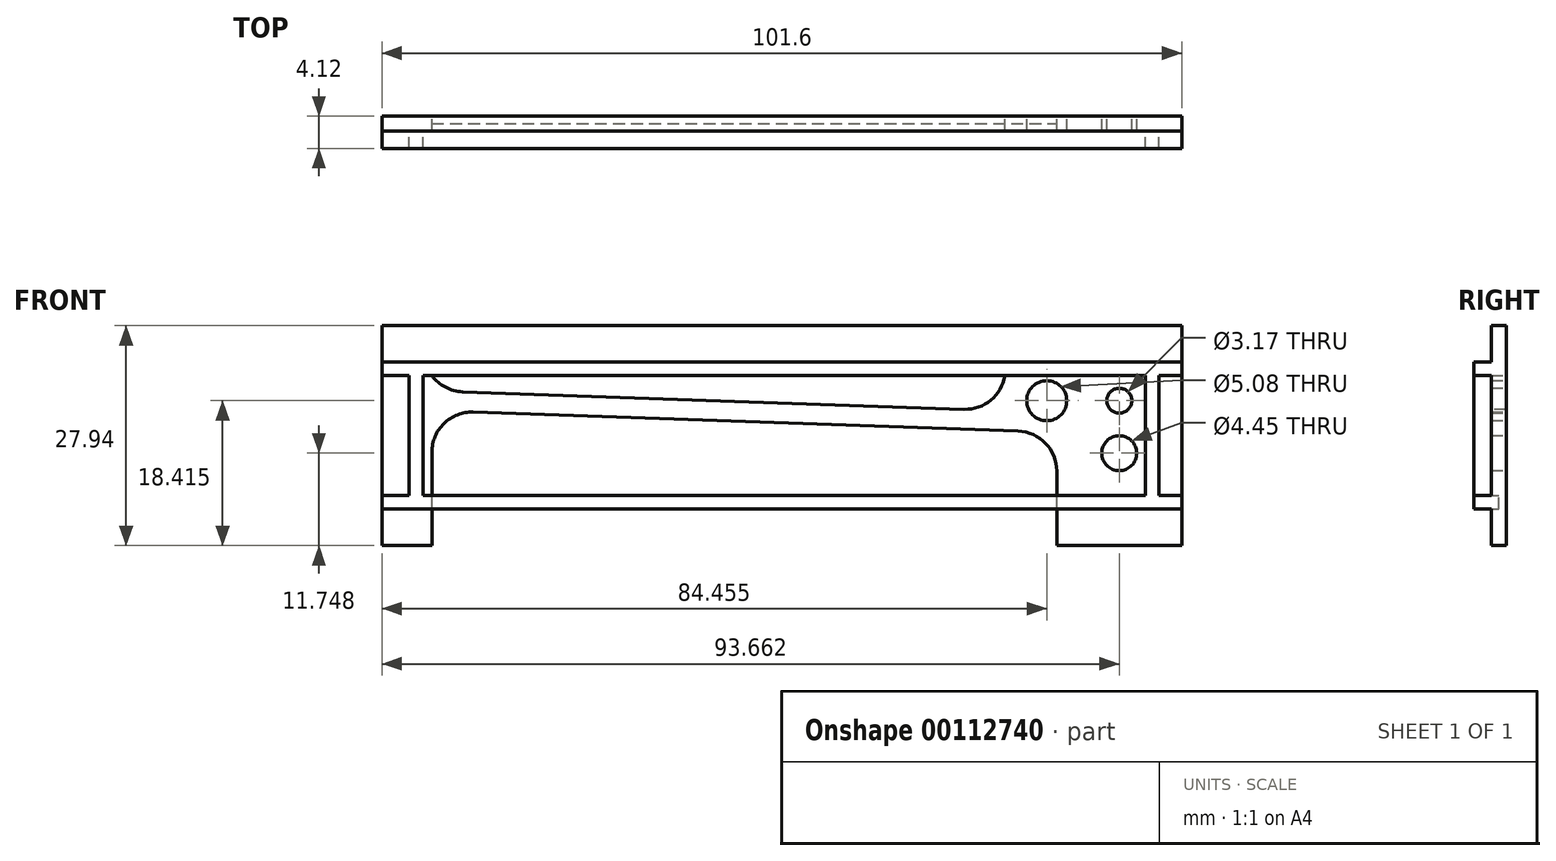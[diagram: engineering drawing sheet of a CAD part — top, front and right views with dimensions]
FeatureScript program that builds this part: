
annotation { "Feature Type Name" : "Feature", "Feature Type Description" : "" }
export const myFeature = defineFeature(function(context is Context, id is Id, definition is map)
    precondition{}
    {
        {
            var Q0;
            Q0=qCreatedBy(makeId("Front.planeOp"),FACE);
            var sketch = newSketch(context, id + "F0", { "sketchPlane" : qUnion([Q0])});
            skLineSegment(sketch, "E0.bottom", {"start": v(-50.8, 0) * mm, "end": v(50.8, 0) * mm});
            skLineSegment(sketch, "E0.top", {"start": v(-50.8, 27.94) * mm, "end": v(50.8, 27.94) * mm});
            skLineSegment(sketch, "E0.left", {"start": v(-50.8, 0) * mm, "end": v(-50.8, 27.94) * mm});
            skLineSegment(sketch, "E0.right", {"start": v(50.8, 0) * mm, "end": v(50.8, 27.94) * mm});
            skLineSegment(sketch, "E1.left", {"start": v(-44.45, 0) * mm, "end": v(-44.45, 17.15) * mm});
            skLineSegment(sketch, "E1.right", {"start": v(34.92, 0) * mm, "end": v(34.92, 14.37) * mm});
            skLineSegment(sketch, "E2", {"start": v(58.26, 4.45) * mm, "end": v(77.64, 4.45) * mm, "construction": true});
            skLineSegment(sketch, "E3", {"start": v(58.26, 23.5) * mm, "end": v(77.64, 23.5) * mm, "construction": true});
            skLineSegment(sketch, "E4", {"start": v(34.93, 14.37) * mm, "end": v(-44.45, 17.14) * mm});
            skLineSegment(sketch, "E5.bottom", {"start": v(-44.45, 0) * mm, "end": v(34.92, 0) * mm});
            skLineSegment(sketch, "E5.top", {"start": v(-44.45, 6.35) * mm, "end": v(34.92, 6.35) * mm});
            skLineSegment(sketch, "E5.left", {"start": v(-44.45, 0) * mm, "end": v(-44.45, 6.35) * mm});
            skLineSegment(sketch, "E5.right", {"start": v(34.92, 0) * mm, "end": v(34.92, 6.35) * mm});
            skLineSegment(sketch, "E6", {"start": v(0, -5.2) * mm, "end": v(0, 26.47) * mm, "construction": true});
            skCircle(sketch, "E7", {"center": v(42.86, 18.42) * mm, "radius": 1.59 * mm});
            skLineSegment(sketch, "E8", {"start": v(28.33, 21.6) * mm, "end": v(-44.45, 21.59) * mm});
            skLineSegment(sketch, "E9", {"start": v(-44.45, 21.59) * mm, "end": v(-44.45, 19.69) * mm});
            skLineSegment(sketch, "E10", {"start": v(-44.45, 19.69) * mm, "end": v(28.33, 17.15) * mm});
            skLineSegment(sketch, "E11", {"start": v(28.33, 17.15) * mm, "end": v(28.33, 21.6) * mm});
            skCircle(sketch, "E12", {"center": v(33.66, 18.42) * mm, "radius": 2.54 * mm});
            skCircle(sketch, "E13", {"center": v(42.86, 11.75) * mm, "radius": 2.22 * mm});
            skSolve(sketch);
        }
        {
            var Q0;
            Q0=makeQuery(id+"F0.imprint","IMPRINT",FACE,{"disambiguationData":[TD([[makeQuery(id+"F0.imprint","IMPRINT",EDGE,{"derivedFrom":sQuery(id+"F0.wireOp",EDGE,"E0.top")}),-1.0]])]});
            var Q1;
            Q1=makeQuery(id+"F0.imprint","IMPRINT",FACE,{"disambiguationData":[TD([[makeQuery(id+"F0.imprint","IMPRINT",EDGE,{"derivedFrom":sQuery(id+"F0.wireOp",EDGE,"FsuTxIii-Xo9e-dLFT-zOUX-yXm8lsklTmyg.bottom")}),-1.0]])]});
            var Q2;
            Q2=makeQuery(id+"F0.imprint","IMPRINT",FACE,{"disambiguationData":[TD([[makeQuery(id+"F0.imprint","IMPRINT",EDGE,{"derivedFrom":sQuery(id+"F0.wireOp",EDGE,"E5.bottom")}),1.0]])]});
            extrude(context, id + "F1", {"entities" : qUnion([Q0, Q1, Q2]), "depth" : 1.9 * mm, "symmetric" : true});
        }
        {
            var Q0;
            Q0=makeQuery(id+"F1.opExtrude","SWEPT_EDGE",EDGE,{"disambiguationData":[OSD([sQuery(id+"F0.wireOp",EDGE,"E1.left"),sQuery(id+"F0.wireOp",EDGE,"E4")])]});
            var Q1;
            Q1=makeQuery(id+"F1.opExtrude","SWEPT_EDGE",EDGE,{"disambiguationData":[OSD([sQuery(id+"F0.wireOp",EDGE,"E1.right"),sQuery(id+"F0.wireOp",EDGE,"E4")])]});
            var Q2;
            Q2=makeQuery(id+"F1.opExtrude","SWEPT_EDGE",EDGE,{"disambiguationData":[OSD([sQuery(id+"F0.wireOp",EDGE,"E9"),sQuery(id+"F0.wireOp",EDGE,"E10")])]});
            var Q3;
            Q3=makeQuery(id+"F1.opExtrude","SWEPT_EDGE",EDGE,{"disambiguationData":[OSD([sQuery(id+"F0.wireOp",EDGE,"E10"),sQuery(id+"F0.wireOp",EDGE,"E11")])]});
            fillet(context, id + "F2", {"entities" : qUnion([Q0, Q1, Q2, Q3]), "radius" : 5.08 * mm, "tangentPropagation" : true, "allowEdgeOverflow" : false});
        }
        {
            var Q0;
            Q0=qCreatedBy(makeId("Front.planeOp"),FACE);
            var sketch = newSketch(context, id + "F3", { "sketchPlane" : qUnion([Q0])});
            skLineSegment(sketch, "E14.bottom", {"start": v(-50.8, 6.35) * mm, "end": v(50.8, 6.35) * mm});
            skLineSegment(sketch, "E14.top", {"start": v(-50.8, 4.64) * mm, "end": v(50.8, 4.64) * mm});
            skLineSegment(sketch, "E14.left", {"start": v(-50.8, 6.35) * mm, "end": v(-50.8, 4.64) * mm});
            skLineSegment(sketch, "E14.right", {"start": v(50.8, 6.35) * mm, "end": v(50.8, 4.64) * mm});
            skLineSegment(sketch, "E15.bottom", {"start": v(-50.8, 21.6) * mm, "end": v(50.8, 21.6) * mm});
            skLineSegment(sketch, "E15.top", {"start": v(-50.8, 23.32) * mm, "end": v(50.8, 23.32) * mm});
            skLineSegment(sketch, "E15.left", {"start": v(-50.8, 21.6) * mm, "end": v(-50.8, 23.32) * mm});
            skLineSegment(sketch, "E15.right", {"start": v(50.8, 21.6) * mm, "end": v(50.8, 23.32) * mm});
            skLineSegment(sketch, "E16.bottom", {"start": v(-47.32, 23.32) * mm, "end": v(-45.6, 23.32) * mm});
            skLineSegment(sketch, "E16.top", {"start": v(-47.32, 4.64) * mm, "end": v(-45.6, 4.64) * mm});
            skLineSegment(sketch, "E16.left", {"start": v(-47.32, 23.32) * mm, "end": v(-47.32, 4.64) * mm});
            skLineSegment(sketch, "E16.right", {"start": v(-45.6, 23.32) * mm, "end": v(-45.6, 4.64) * mm});
            skLineSegment(sketch, "E17.bottom", {"start": v(46.16, 23.32) * mm, "end": v(47.88, 23.32) * mm});
            skLineSegment(sketch, "E17.top", {"start": v(46.16, 4.64) * mm, "end": v(47.88, 4.64) * mm});
            skLineSegment(sketch, "E17.left", {"start": v(46.16, 23.32) * mm, "end": v(46.16, 4.64) * mm});
            skLineSegment(sketch, "E17.right", {"start": v(47.88, 23.32) * mm, "end": v(47.88, 4.64) * mm});
            skSolve(sketch);
        }
        {
            var Q0;
            Q0 = qSketchRegion(id + "F3", true);
            extrude(context, id + "F4", {"entities" : qUnion([Q0]), "operationType" : NewBodyOperationType.ADD, "depth" : 3.17 * mm});
        }
    });
